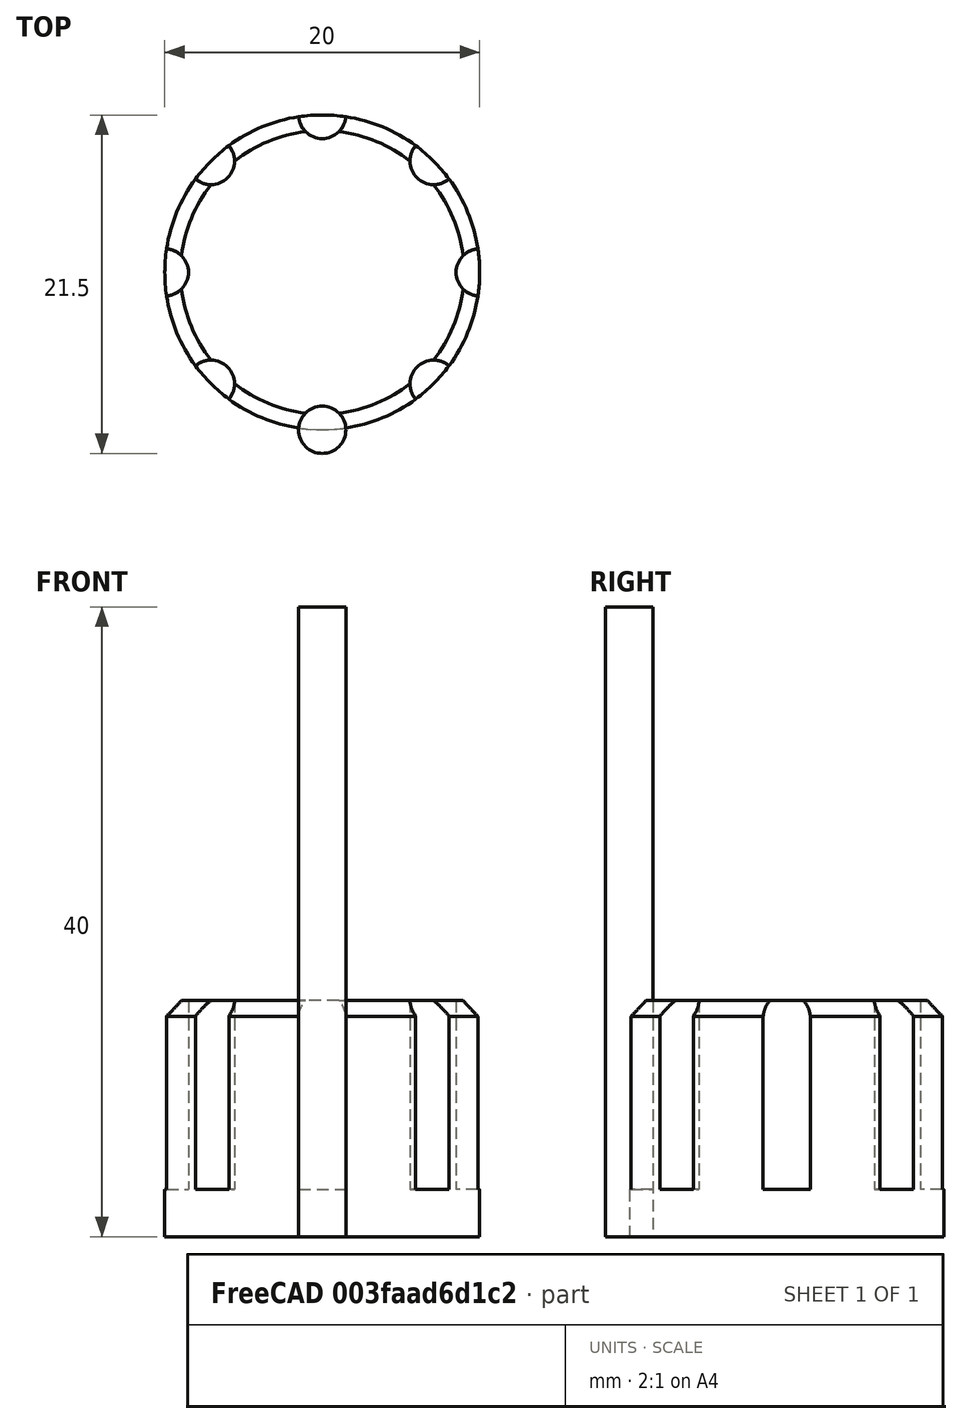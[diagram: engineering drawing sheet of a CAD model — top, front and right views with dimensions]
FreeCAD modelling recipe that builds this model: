
FCSTD DOCUMENT  (FreeCAD 1.0R39319 (Git))
Label: ojt1_t12r01_buttom.potencioner
License: All rights reserved
LicenseURL: https://en.wikipedia.org/wiki/All_rights_reserved
objects: Part::Chamfer×8, Part::Cylinder×2, Part::FeaturePython×1, Part::Cut×1
note: 11 computed .brp shape members not serialized (recipe doc carries the construction recipe); baked Part::Feature solids carry a one-line shape summary decoded from their .brp

FEATURE [Part::Cylinder] Cylinder002  label="Cilindre002"
  Angle = 360
  AttacherType = Attacher::AttachEngine3D
  FirstAngle = 0
  Height = 15
  Placement = pos=(0,10,0) rot=(0,0,1;0rad)
  Radius = 10
  SecondAngle = 0
FEATURE [Part::Cylinder] Cylinder003  label="Cilindre003"
  Angle = 360
  AttacherType = Attacher::AttachEngine3D
  FirstAngle = 0
  Height = 40
  Radius = 1.5
  SecondAngle = 0
FEATURE [Part::FeaturePython] Array001  # Draft array (typed FeaturePython)
  AlwaysSyncPlacement = false
  Angle = 360
  ArrayType = 1
  Axis = (0,0,1)
  Base = -> Cylinder003
  Center = (0,10,0)
  Count = 8
  ExpandArray = false
  Fuse = false
  IntervalAxis = (0,0,0)
  IntervalX = (50,0,0)
  IntervalY = (0,50,0)
  IntervalZ = (0,0,50)
  NumberCircles = 3
  NumberPolar = 8
  NumberX = 2
  NumberY = 2
  NumberZ = 1
  Placement = pos=(0,0,3) rot=(0,0,1;0rad)
  PlacementList = 8 placements: [(0,0,0),(7.07107,2.92893,0),(10,10,0),(7.07107,17.0711,0),(1.22465e-15,20,0),(-7.07107,17.0711,0),(-10,10,0),(-7.07107,2.92893,0)]
  RadialDistance = 50
  ScaleList = (8) [(1,1,1),(1,1,1),(1,1,1),(1,1,1),(1,1,1),(1,1,1),(1,1,1),(1,1,1)]
  Symmetry = 1
  TangentialDistance = 25
FEATURE [Part::Cut] Cut001
  Base = -> Cylinder002
  Refine = true
  Tool = -> Array001
FEATURE [Part::Chamfer] Chamfer
  Base = -> Cut001
  EdgeLinks = -> Cut001 [Edge13]
  Edges = 1 edges r=1: [Edge13]
FEATURE [Part::Chamfer] Chamfer001
  Base = -> Chamfer
  EdgeLinks = -> Chamfer [Edge7]
  Edges = 1 edges r=1: [Edge7]
FEATURE [Part::Chamfer] Chamfer002
  Base = -> Chamfer001
  EdgeLinks = -> Chamfer001 [Edge15]
  Edges = 1 edges r=1: [Edge15]
FEATURE [Part::Chamfer] Chamfer003
  Base = -> Chamfer002
  EdgeLinks = -> Chamfer002 [Edge23]
  Edges = 1 edges r=1: [Edge23]
FEATURE [Part::Chamfer] Chamfer004
  Base = -> Chamfer003
  EdgeLinks = -> Chamfer003 [Edge17]
  Edges = 1 edges r=1: [Edge17]
FEATURE [Part::Chamfer] Chamfer005
  Base = -> Chamfer004
  EdgeLinks = -> Chamfer004 [Edge9]
  Edges = 1 edges r=1: [Edge9]
FEATURE [Part::Chamfer] Chamfer006
  Base = -> Chamfer005
  EdgeLinks = -> Chamfer005 [Edge17]
  Edges = 1 edges r=1: [Edge17]
FEATURE [Part::Chamfer] Chamfer007
  Base = -> Chamfer006
  EdgeLinks = -> Chamfer006 [Edge7]
  Edges = 1 edges r=1: [Edge7]
